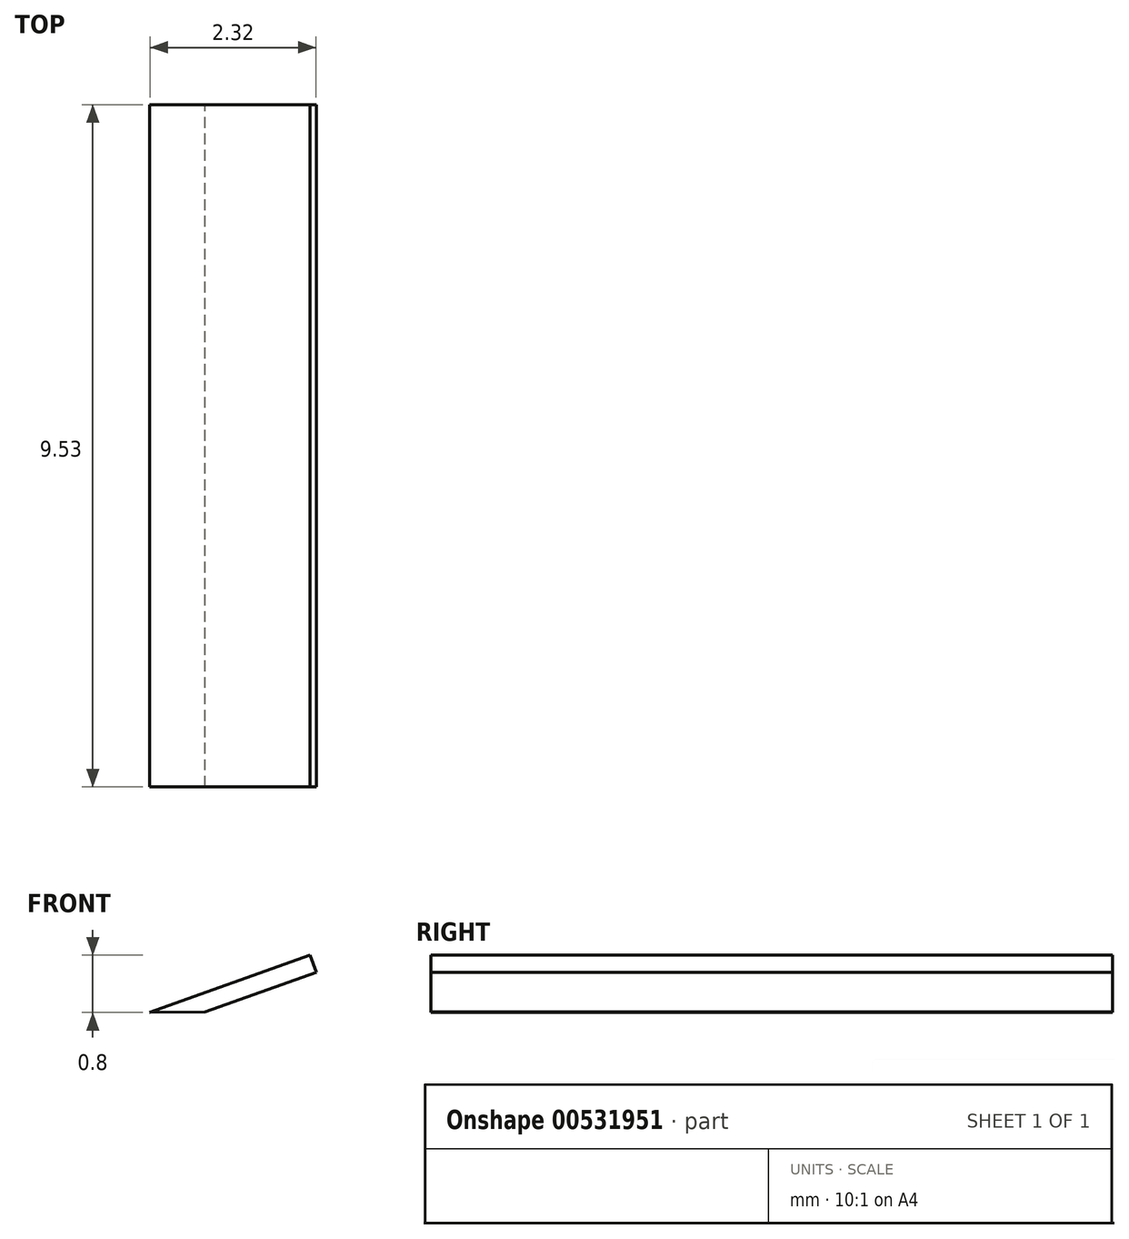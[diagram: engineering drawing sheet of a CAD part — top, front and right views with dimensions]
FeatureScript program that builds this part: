
annotation { "Feature Type Name" : "Feature", "Feature Type Description" : "" }
export const myFeature = defineFeature(function(context is Context, id is Id, definition is map)
    precondition{}
    {
        {
            var Q0;
            Q0=qCreatedBy(makeId("Front.planeOp"),FACE);
            var sketch = newSketch(context, id + "F0", { "sketchPlane" : qUnion([Q0])});
            skLineSegment(sketch, "E0", {"start": v(12.27, 8.2) * mm, "end": v(14.5, 9) * mm});
            skLineSegment(sketch, "E1", {"start": v(14.5, 9) * mm, "end": v(14.6, 8.75) * mm});
            skLineSegment(sketch, "E2", {"start": v(14.6, 8.75) * mm, "end": v(13.04, 8.2) * mm});
            skLineSegment(sketch, "E3", {"start": v(12.27, 8.2) * mm, "end": v(13.04, 8.2) * mm});
            skSolve(sketch);
        }
        {
            var Q0;
            Q0 = qSketchRegion(id + "F0", true);
            extrude(context, id + "F1", {"entities" : qUnion([Q0]), "depth" : 9.52 * mm, "offsetDistance" : 25.4 * mm});
        }
    });
